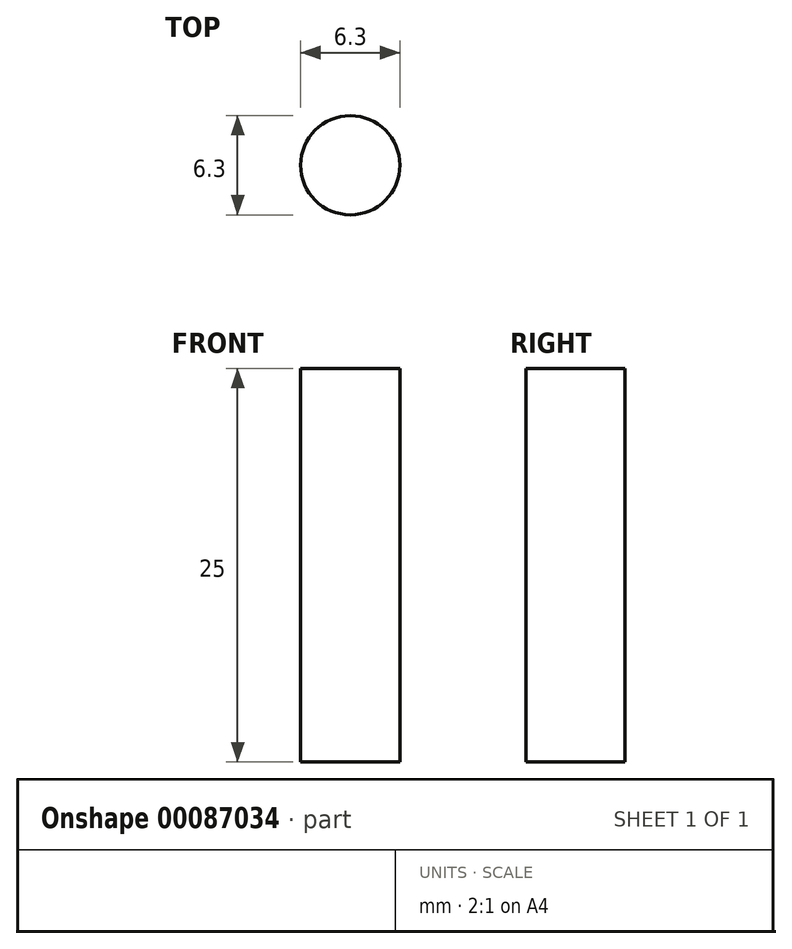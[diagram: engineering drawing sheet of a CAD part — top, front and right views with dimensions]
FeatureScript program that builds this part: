
annotation { "Feature Type Name" : "Feature", "Feature Type Description" : "" }
export const myFeature = defineFeature(function(context is Context, id is Id, definition is map)
    precondition{}
    {
        {
            var Q0;
            Q0=qCreatedBy(makeId("Top.planeOp"),FACE);
            var sketch = newSketch(context, id + "F0", { "sketchPlane" : qUnion([Q0])});
            skCircle(sketch, "E0", {"center": v(0, 0) * mm, "radius": 3.15 * mm});
            skSolve(sketch);
        }
        {
            var Q0;
            Q0=makeQuery(id+"F0.imprint","IMPRINT",FACE,{"disambiguationData":[TD([[makeQuery(id+"F0.imprint","IMPRINT",EDGE,{"derivedFrom":sQuery(id+"F0.wireOp",EDGE,"E0")}),1.0]])]});
            extrude(context, id + "F1", {"entities" : qUnion([Q0]), "depth" : 25 * mm});
        }
    });
